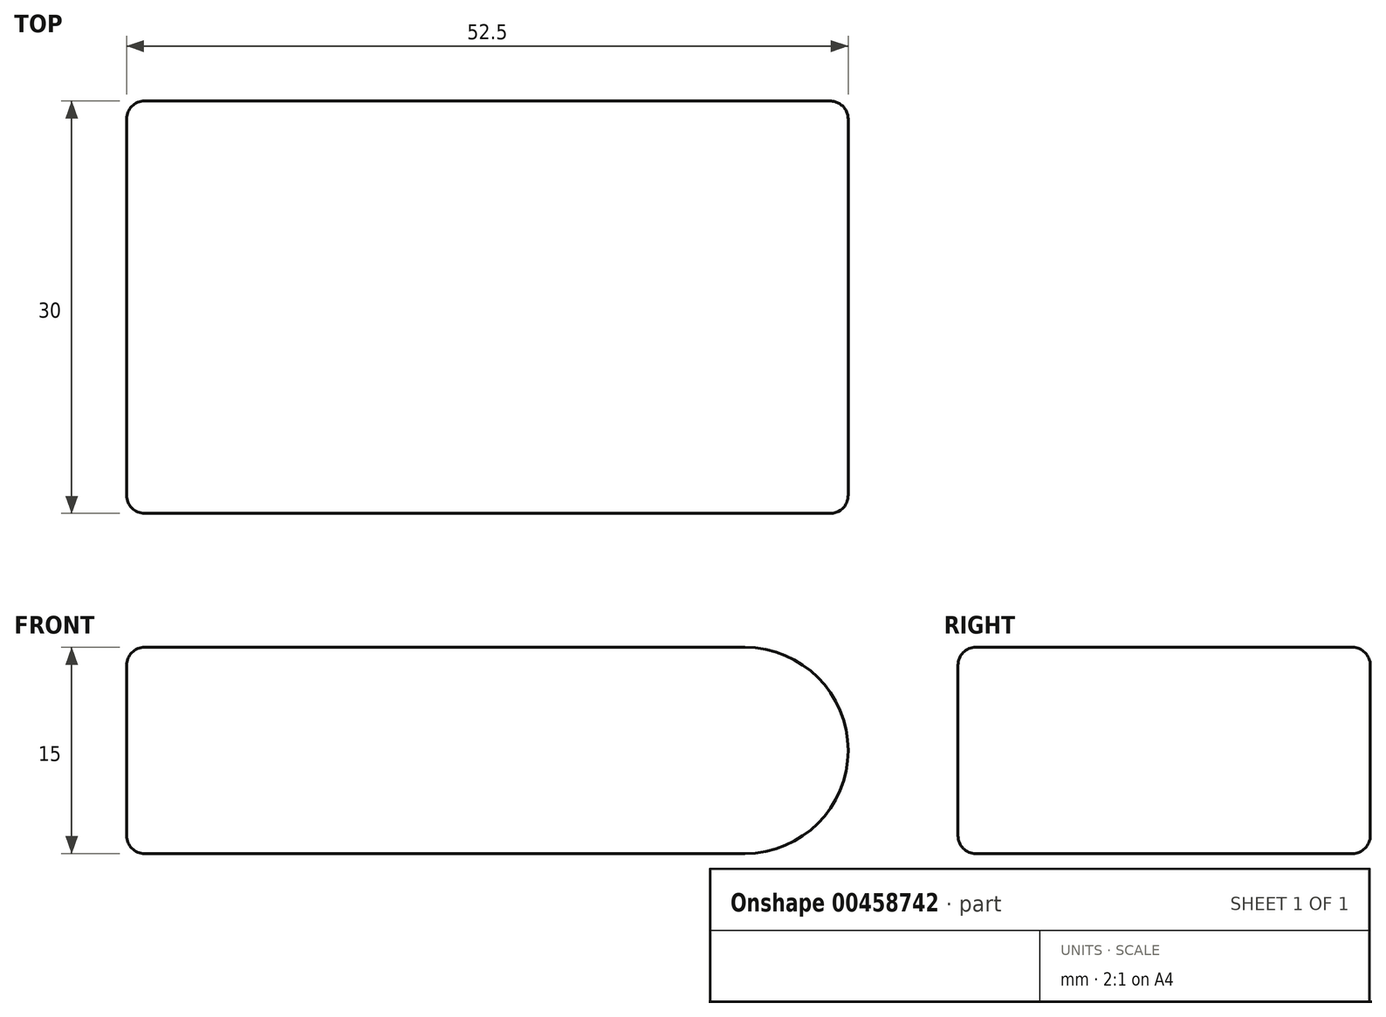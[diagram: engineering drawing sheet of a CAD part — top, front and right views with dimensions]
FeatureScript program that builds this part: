
annotation { "Feature Type Name" : "Feature", "Feature Type Description" : "" }
export const myFeature = defineFeature(function(context is Context, id is Id, definition is map)
    precondition{}
    {
        {
            var Q0;
            Q0=qCreatedBy(makeId("Top.planeOp"),FACE);
            var sketch = newSketch(context, id + "F0", { "sketchPlane" : qUnion([Q0])});
            skLineSegment(sketch, "E0.bottom", {"start": v(22.5, -15) * mm, "end": v(-22.5, -15) * mm});
            skLineSegment(sketch, "E0.top", {"start": v(22.5, 15) * mm, "end": v(-22.5, 15) * mm});
            skLineSegment(sketch, "E0.left", {"start": v(22.5, -15) * mm, "end": v(22.5, 15) * mm});
            skLineSegment(sketch, "E0.right", {"start": v(-22.5, -15) * mm, "end": v(-22.5, 15) * mm});
            skPoint(sketch, "E0.middle", {"position": v(0, 0) * mm});
            skSolve(sketch);
        }
        {
            var Q0;
            Q0 = qSketchRegion(id + "F0", true);
            extrude(context, id + "F1", {"entities" : qUnion([Q0]), "depth" : 15 * mm, "offsetDistance" : 25 * mm});
        }
        {
            var Q0;
            Q0=makeQuery(id+"F1.opExtrude","SWEPT_FACE",FACE,{"disambiguationData":[OSD([sQuery(id+"F0.wireOp",EDGE,"E0.bottom")])]});
            var sketch = newSketch(context, id + "F2", { "sketchPlane" : qUnion([Q0])});
            skArc(sketch, "E1", {"start": v(22.5, 0) * mm, "mid": v(30, 7.5) * mm, "end": v(22.5, 15) * mm});
            skSolve(sketch);
        }
        {
            var Q0;
            Q0=makeQuery(id+"F2.imprint","IMPRINT",FACE,{"disambiguationData":[TD([[makeQuery(id+"F2.imprint","IMPRINT",EDGE,{"derivedFrom":sQuery(id+"F2.wireOp",EDGE,"E1")}),1.0]])]});
            var Q1;
            Q1=makeQuery(id+"F1.opExtrude","SWEPT_FACE",FACE,{"disambiguationData":[OSD([sQuery(id+"F0.wireOp",EDGE,"E0.top")])]});
            extrude(context, id + "F3", {"entities" : qUnion([Q0]), "operationType" : NewBodyOperationType.ADD, "endBound" : BoundingType.UP_TO_SURFACE, "oppositeDirection" : true, "depth" : 25 * mm, "endBoundEntityFace" : qUnion([Q1]), "offsetDistance" : 25 * mm});
        }
        {
            var Q0;
            Q0=makeQuery(id+"F3.opExtrude","CAP_EDGE",EDGE,{"disambiguationData":[OSD([sQuery(id+"F2.wireOp",EDGE,"E1")])],"isStart":false});
            var Q1;
            Q1=makeQuery(id+"F1.opExtrude","CAP_EDGE",EDGE,{"disambiguationData":[OSD([sQuery(id+"F0.wireOp",EDGE,"E0.top")])],"isStart":true});
            var Q2;
            Q2=makeQuery(id+"F1.opExtrude","CAP_EDGE",EDGE,{"disambiguationData":[OSD([sQuery(id+"F0.wireOp",EDGE,"E0.top")])],"isStart":false});
            var Q3;
            {var subQ0=sQuery(id+"F2.wireOp",EDGE,"E1");var subQ1=sQuery(id+"F0.wireOp",EDGE,"E0.bottom");var subQ2=sQuery(id+"F0.wireOp",EDGE,"E0.left");Q3=makeQuery(id+"F3.boolean.opBoolean","MERGE",EDGE,{"derivedFrom":[makeQuery(id+"F1.opExtrude","CAP_EDGE",EDGE,{"disambiguationData":[OSD([subQ2])],"isStart":false}),makeQuery(id+"F3.opExtrude","SWEPT_EDGE",EDGE,{"disambiguationData":[OSD([subQ1,subQ2,subQ0]),TDD([makeQuery(id+"F2.imprint","INTERSECT",VERTEX,{"derivedFrom":[makeQuery(id+"F1.opExtrude","SWEPT_EDGE",EDGE,{"disambiguationData":[OSD([subQ1,subQ2])]}),makeQuery(id+"F1.opExtrude","CAP_EDGE",EDGE,{"disambiguationData":[OSD([subQ1])],"isStart":false}),subQ0]})])]})]});}
            var Q4;
            Q4=makeQuery(id+"F1.opExtrude","CAP_EDGE",EDGE,{"disambiguationData":[OSD([sQuery(id+"F0.wireOp",EDGE,"E0.right")])],"isStart":false});
            var Q5;
            Q5=makeQuery(id+"F1.opExtrude","CAP_EDGE",EDGE,{"disambiguationData":[OSD([sQuery(id+"F0.wireOp",EDGE,"E0.bottom")])],"isStart":true});
            var Q6;
            Q6=makeQuery(id+"F1.opExtrude","CAP_EDGE",EDGE,{"disambiguationData":[OSD([sQuery(id+"F0.wireOp",EDGE,"E0.bottom")])],"isStart":false});
            var Q7;
            Q7=makeQuery(id+"F1.opExtrude","CAP_EDGE",EDGE,{"disambiguationData":[OSD([sQuery(id+"F0.wireOp",EDGE,"E0.right")])],"isStart":true});
            var Q8;
            Q8=makeQuery(id+"F1.opExtrude","SWEPT_EDGE",EDGE,{"disambiguationData":[OSD([sQuery(id+"F0.wireOp",EDGE,"E0.bottom"),sQuery(id+"F0.wireOp",EDGE,"E0.right")])]});
            var Q9;
            Q9=makeQuery(id+"F1.opExtrude","SWEPT_EDGE",EDGE,{"disambiguationData":[OSD([sQuery(id+"F0.wireOp",EDGE,"E0.top"),sQuery(id+"F0.wireOp",EDGE,"E0.right")])]});
            var Q10;
            {var subQ0=sQuery(id+"F2.wireOp",EDGE,"E1");var subQ1=sQuery(id+"F0.wireOp",EDGE,"E0.bottom");var subQ2=sQuery(id+"F0.wireOp",EDGE,"E0.left");Q10=makeQuery(id+"F3.boolean.opBoolean","MERGE",EDGE,{"derivedFrom":[makeQuery(id+"F1.opExtrude","CAP_EDGE",EDGE,{"disambiguationData":[OSD([subQ2])],"isStart":true}),makeQuery(id+"F3.opExtrude","SWEPT_EDGE",EDGE,{"disambiguationData":[OSD([subQ1,subQ2,subQ0]),TDD([makeQuery(id+"F2.imprint","INTERSECT",VERTEX,{"derivedFrom":[makeQuery(id+"F1.opExtrude","SWEPT_EDGE",EDGE,{"disambiguationData":[OSD([subQ1,subQ2])]}),makeQuery(id+"F1.opExtrude","CAP_EDGE",EDGE,{"disambiguationData":[OSD([subQ1])],"isStart":true}),subQ0]})])]})]});}
            var Q11;
            Q11=makeQuery(id+"F3.opExtrude","CAP_EDGE",EDGE,{"disambiguationData":[OSD([sQuery(id+"F2.wireOp",EDGE,"E1")])],"isStart":true});
            fillet(context, id + "F4", {"entities" : qUnion([Q0, Q1, Q2, Q3, Q4, Q5, Q6, Q7, Q8, Q9, Q10, Q11]), "radius" : 1.3 * mm, "tangentPropagation" : true, "allowEdgeOverflow" : false});
        }
    });
